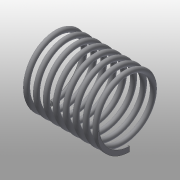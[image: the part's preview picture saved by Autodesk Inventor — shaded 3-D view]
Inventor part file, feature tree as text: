
AUTODESK INVENTOR PART (.ipt)
format: ipt  version: 2015 (Build 190159000, 159)  size: 356,352 bytes
history: native  units: mm
features: other x3, sketch x2
ambient origin geometry x8: Origin, YZ Plane, XZ Plane, XY Plane, X Axis, Y Axis, Z Axis, Center Point
bodies: Solid1 (feature_tree)
feature tree (5):
  other  "Compression Spring 16.ipt"
  other  "Solid1::Compression Spring 16.ipt"
  other  "TaggingFeature1"
  sketch  "Sketch1"  dims[d0=10.0mm]
  sketch  "Sketch2"
